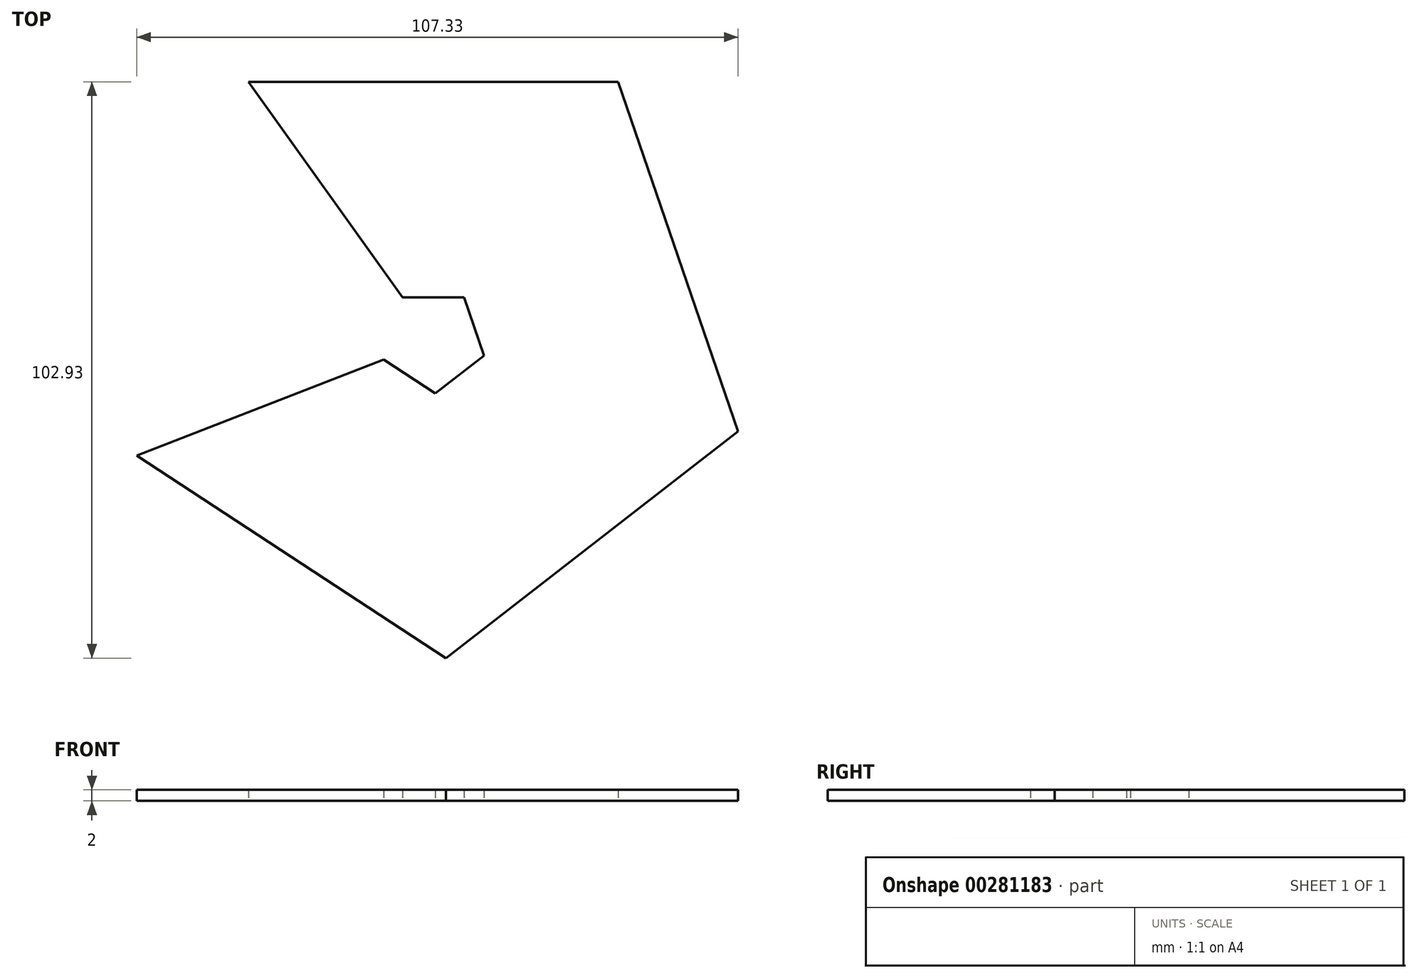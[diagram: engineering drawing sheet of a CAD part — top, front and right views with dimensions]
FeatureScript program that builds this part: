
annotation { "Feature Type Name" : "Feature", "Feature Type Description" : "" }
export const myFeature = defineFeature(function(context is Context, id is Id, definition is map)
    precondition{}
    {
        {
            var Q0;
            Q0=qCreatedBy(makeId("Top.planeOp"),FACE);
            var sketch = newSketch(context, id + "F0", { "sketchPlane" : qUnion([Q0])});
            skLineSegment(sketch, "E0", {"start": v(-5.5, 0) * mm, "end": v(5.5, 0) * mm});
            skLineSegment(sketch, "E1", {"start": v(-5.5, 0) * mm, "end": v(-33, 38.5) * mm});
            skLineSegment(sketch, "E2", {"start": v(-33, 38.5) * mm, "end": v(0, 38.5) * mm});
            skLineSegment(sketch, "E3.MirrorCS", {"start": v(5.5, 0) * mm, "end": v(33, 38.5) * mm});
            skLineSegment(sketch, "E4.MirrorCS", {"start": v(33, 38.5) * mm, "end": v(0, 38.5) * mm});
            skLineSegment(sketch, "E5.MirrorCS", {"start": v(33, 38.5) * mm, "end": v(43.7, 7.28) * mm});
            skLineSegment(sketch, "E6.MirrorCS", {"start": v(54.4, -23.93) * mm, "end": v(43.7, 7.28) * mm});
            skLineSegment(sketch, "E7.MirrorCS", {"start": v(9.07, -10.4) * mm, "end": v(54.4, -23.93) * mm});
            skLineSegment(sketch, "E8.MirrorCS", {"start": v(9.07, -10.4) * mm, "end": v(5.5, 0) * mm});
            skLineSegment(sketch, "E9.MirrorCS", {"start": v(9.07, -10.4) * mm, "end": v(0.38, -17.15) * mm});
            skLineSegment(sketch, "E10.MirrorCS", {"start": v(54.4, -23.93) * mm, "end": v(28.35, -44.18) * mm});
            skLineSegment(sketch, "E11.MirrorCS", {"start": v(2.29, -64.43) * mm, "end": v(28.35, -44.18) * mm});
            skLineSegment(sketch, "E12.MirrorCS", {"start": v(0.38, -17.15) * mm, "end": v(2.29, -64.43) * mm});
            skLineSegment(sketch, "E13.MirrorCS", {"start": v(-8.82, -11.13) * mm, "end": v(0.38, -17.15) * mm});
            skLineSegment(sketch, "E14.MirrorCS", {"start": v(2.29, -64.43) * mm, "end": v(-25.32, -46.35) * mm});
            skLineSegment(sketch, "E15.MirrorCS", {"start": v(-52.92, -28.26) * mm, "end": v(-25.32, -46.35) * mm});
            skLineSegment(sketch, "E16.MirrorCS", {"start": v(-8.82, -11.13) * mm, "end": v(-52.92, -28.26) * mm});
            skSolve(sketch);
        }
        {
            var Q0;
            Q0=makeQuery(id+"F0.imprint","IMPRINT",FACE,{"disambiguationData":[TD([[makeQuery(id+"F0.imprint","IMPRINT",EDGE,{"derivedFrom":sQuery(id+"F0.wireOp",EDGE,"E7.MirrorCS")}),-1.0]])]});
            var Q1;
            Q1=makeQuery(id+"F0.imprint","IMPRINT",FACE,{"disambiguationData":[TD([[makeQuery(id+"F0.imprint","IMPRINT",EDGE,{"derivedFrom":sQuery(id+"F0.wireOp",EDGE,"E12.MirrorCS")}),-1.0]])]});
            var Q2;
            Q2=makeQuery(id+"F0.imprint","IMPRINT",FACE,{"disambiguationData":[TD([[makeQuery(id+"F0.imprint","IMPRINT",EDGE,{"derivedFrom":sQuery(id+"F0.wireOp",EDGE,"E3.MirrorCS")}),-1.0]])]});
            var Q3;
            Q3=makeQuery(id+"F0.imprint","IMPRINT",FACE,{"disambiguationData":[TD([[makeQuery(id+"F0.imprint","IMPRINT",EDGE,{"derivedFrom":sQuery(id+"F0.wireOp",EDGE,"E0")}),1.0]])]});
            extrude(context, id + "F1", {"entities" : qUnion([Q0, Q1, Q2, Q3]), "depth" : 2 * mm});
        }
    });
